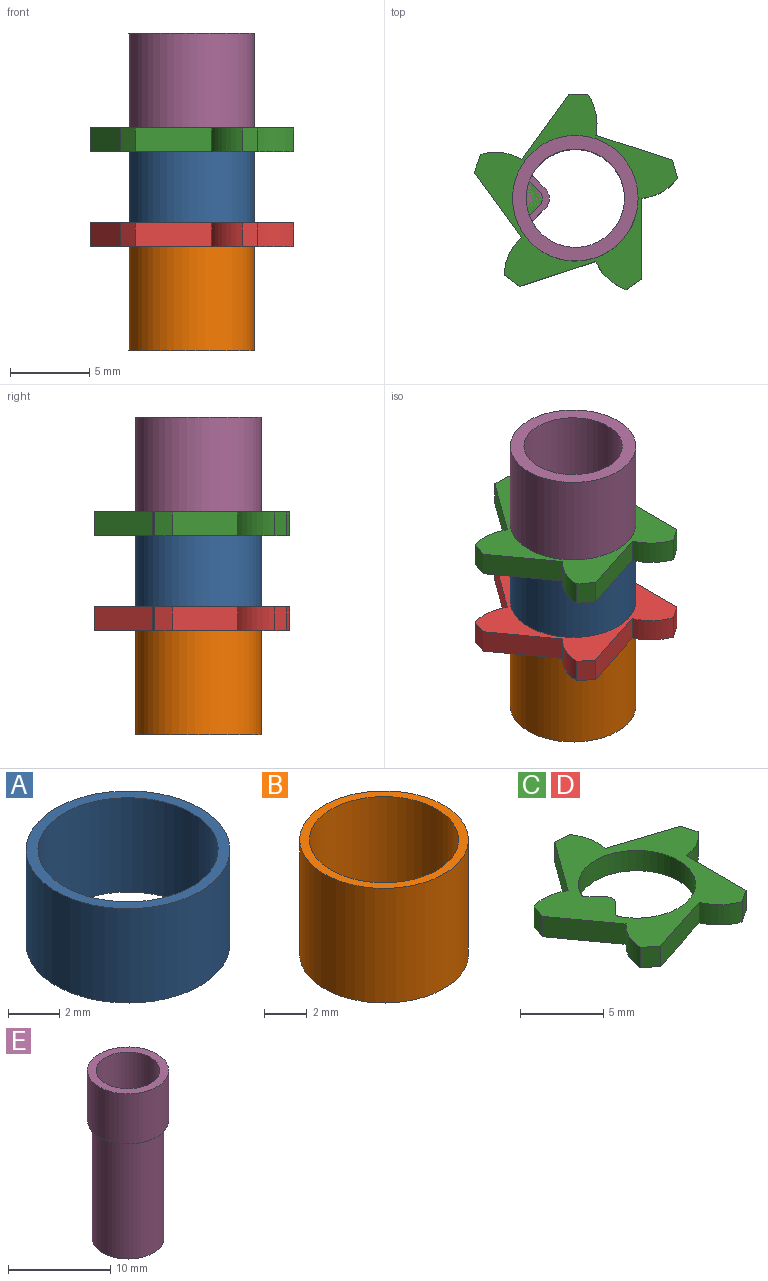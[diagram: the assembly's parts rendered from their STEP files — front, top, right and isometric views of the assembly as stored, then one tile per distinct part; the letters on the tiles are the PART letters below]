
ASSEMBLY  parts=5 mates=3
PART A: 4 faces, bbox 7.9x7.9x4.5 mm
  f0: cylinder r=3.51mm len=7.02mm, axis (0,0,-1), area 99.2mm2, adj f2,f3
  f1: cylinder r=3.97mm len=7.94mm, axis (0,0,-1), area 112.2mm2, adj f2,f3
  f2: plane 7.94x7.94mm, normal (0,0,1), area 10.8mm2, adj f0,f1
  f3: plane 7.94x7.94mm, normal (0,0,-1), area 10.8mm2, adj f0,f1
PART B: 4 faces, bbox 7.9x7.9x6.6 mm
  f0: cylinder r=3.51mm len=7.02mm, axis (0,0,-1), area 145.5mm2, adj f2,f3
  f1: cylinder r=3.97mm len=7.94mm, axis (0,0,-1), area 164.6mm2, adj f2,f3
  f2: plane 7.94x7.94mm, normal (0,0,1), area 10.8mm2, adj f0,f1
  f3: plane 7.94x7.94mm, normal (0,0,-1), area 10.8mm2, adj f0,f1
PART C: 23 faces, bbox 12.9x12.4x1.5 mm
  f0: plane 5.09x1.5mm, normal (1,0,0), area 7.6mm2, adj f1,f20,f21,f22
  f1: cylinder r=3.29mm len=2.28mm, axis (0,0,-1), area 4mm2, adj f0,f2,f21,f22
  f2: plane 1.5x1.15mm, normal (0.96,0.28,0), area 1.8mm2, adj f1,f3,f21,f22
  f3: plane 4.84x1.57mm, normal (0.31,0.95,0), area 7.6mm2, adj f2,f4,f21,f22
  f4: cylinder r=3.29mm len=2.56mm, axis (0,0,-1), area 4mm2, adj f3,f5,f21,f22
  f5: plane 1.5x1.2mm, normal (0.03,1,0), area 1.8mm2, adj f4,f6,f21,f22
  f6: plane 4.12x2.99mm, normal (-0.81,0.59,0), area 7.6mm2, adj f5,f7,f21,f22
  f7: cylinder r=3.29mm len=2.59mm, axis (0,0,-1), area 4mm2, adj f6,f8,f21,f22
  f8: plane 1.5x1.13mm, normal (-0.94,0.34,0), area 1.8mm2, adj f7,f9,f21,f22
  f9: plane 4.12x2.99mm, normal (-0.81,-0.59,0), area 7.6mm2, adj f8,f10,f21,f22
  f10: cylinder r=3.29mm len=2.37mm, axis (0,0,-1), area 4mm2, adj f9,f11,f21,f22
  f11: plane 1.5x0.95mm, normal (-0.61,-0.79,0), area 1.8mm2, adj f10,f12,f21,f22
  f12: plane 4.84x1.57mm, normal (0.31,-0.95,0), area 7.6mm2, adj f11,f13,f21,f22
  f13: cylinder r=3.29mm len=1.91mm, axis (0,0,-1), area 4mm2, adj f12,f20,f21,f22
  f14: cylinder r=3.53mm len=7.06mm, axis (0,0,-1), area 28.3mm2, adj f15,f19,f21,f22
  f15: cylinder r=0.3mm len=1.5mm, axis (0,0,-1), area 0.6mm2, adj f14,f16,f21,f22
  f16: plane 1.5x0.83mm, normal (0.71,-0.71,0), area 1.8mm2, adj f15,f17,f21,f22
  f17: cylinder r=0.6mm len=1.5mm, axis (0,0,-1), area 1.4mm2, adj f16,f18,f21,f22
  f18: plane 1.5x0.83mm, normal (0.71,0.71,0), area 1.8mm2, adj f17,f19,f21,f22
  f19: cylinder r=0.3mm len=1.5mm, axis (0,0,-1), area 0.6mm2, adj f14,f18,f21,f22
  f20: plane 1.5x0.99mm, normal (0.56,-0.83,0), area 1.8mm2, adj f0,f13,f21,f22
  f21: plane 12.87x12.36mm, normal (0,0,1), area 52.2mm2, adj f0,f1,f2,f3,f4,f5,f6,f7
  f22: plane 12.87x12.36mm, normal (0,0,-1), area 52.2mm2, adj f0,f1,f2,f3,f4,f5,f6,f7
PART D: same geometry as C
PART E: 12 faces, bbox 7.9x7.9x20.1 mm
  f0: cylinder r=3.11mm len=20.1mm, axis (0,0,-1), area 346.2mm2, adj f2,f4,f5,f9,f11
  f1: cylinder r=3.97mm len=7.94mm, axis (0,0,-1), area 149.7mm2, adj f2,f3
  f2: plane 7.94x7.94mm, normal (0,0,1), area 19.2mm2, adj f0,f1
  f3: plane 7.94x7.94mm, normal (0,0,-1), area 10.8mm2, adj f1,f10
  f4: plane 3.13x1.46mm, normal (0,0,1), area 2.7mm2, adj f0,f5,f6,f7,f8,f9
  f5: cylinder r=0.15mm len=14.1mm, axis (0,0,1), area 2.8mm2, adj f0,f4,f6,f11
  f6: plane 14.1x0.75mm, normal (0.71,0.71,0), area 14.9mm2, adj f4,f5,f7,f11
  f7: cylinder r=0.9mm len=14.1mm, axis (0,0,1), area 19.9mm2, adj f4,f6,f8,f11
  f8: plane 14.1x0.75mm, normal (0.71,-0.71,0), area 14.9mm2, adj f4,f7,f9,f11
  f9: cylinder r=0.15mm len=14.1mm, axis (0,0,1), area 2.8mm2, adj f0,f4,f8,f11
  f10: cylinder r=3.51mm len=14.1mm, axis (0,0,1), area 310.9mm2, adj f3,f11
  f11: plane 7.02x7.02mm, normal (0,0,-1), area 11mm2, adj f0,f5,f6,f7,f8,f9,f10
PLACE A t=(0,0,-6)mm
PLACE B t=(0,0,-14.1)mm
PLACE C t=(0,0,-1.5)mm
PLACE D t=(0,0,-7.5)mm
PLACE E at identity fixed
MATE fastened C.f14 <-> A.f0  axis (0,0,-1) through (0,0,-1.5)mm
MATE fastened D.f14 <-> A.f0  axis (0,0,-1) through (0,0,-6)mm
MATE fastened B.f0 <-> D.f14  axis (0,0,-1) through (0,0,-7.5)mm
